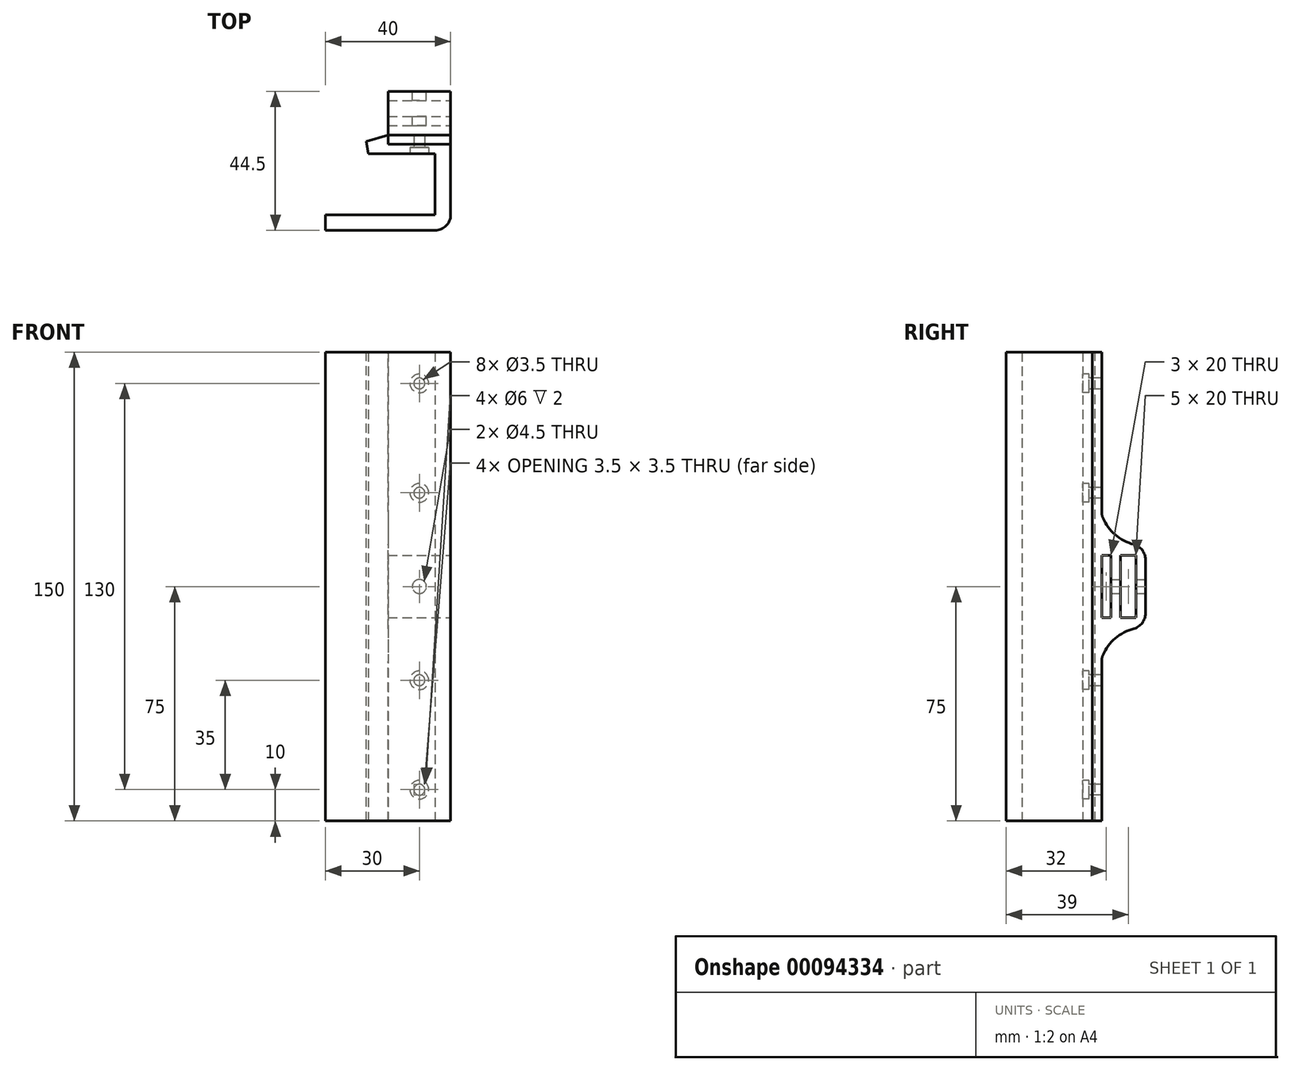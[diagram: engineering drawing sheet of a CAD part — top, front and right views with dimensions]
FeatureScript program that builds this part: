
annotation { "Feature Type Name" : "Feature", "Feature Type Description" : "" }
export const myFeature = defineFeature(function(context is Context, id is Id, definition is map)
    precondition{}
    {
        {
            var Q0;
            Q0=qCreatedBy(makeId("Top.planeOp"),FACE);
            var sketch = newSketch(context, id + "F0", { "sketchPlane" : qUnion([Q0])});
            skLineSegment(sketch, "E0", {"start": v(40, 0) * mm, "end": v(40, 27.5) * mm});
            skLineSegment(sketch, "E1", {"start": v(35, 24.5) * mm, "end": v(35, 5) * mm});
            skLineSegment(sketch, "E2", {"start": v(0, 0) * mm, "end": v(40, 0) * mm});
            skLineSegment(sketch, "E3", {"start": v(35, 5) * mm, "end": v(0, 5) * mm});
            skLineSegment(sketch, "E4", {"start": v(0, 5) * mm, "end": v(0, 0) * mm});
            skLineSegment(sketch, "E5", {"start": v(35, 24.5) * mm, "end": v(20, 24.5) * mm});
            skLineSegment(sketch, "E6", {"start": v(20, 24.5) * mm, "end": v(20, 27.5) * mm, "construction": true});
            skLineSegment(sketch, "E7", {"start": v(20, 27.5) * mm, "end": v(40, 27.5) * mm});
            skLineSegment(sketch, "E8", {"start": v(20, 24.5) * mm, "end": v(0, 24.5) * mm});
            skLineSegment(sketch, "E9", {"start": v(20, 27.5) * mm, "end": v(20, 30.5) * mm});
            skLineSegment(sketch, "E10", {"start": v(20, 30.5) * mm, "end": v(0, 24.5) * mm});
            skSolve(sketch);
        }
        {
            var Q0;
            Q0 = qSketchRegion(id + "F0", true);
            extrude(context, id + "F1", {"entities" : qUnion([Q0]), "depth" : 150 * mm});
        }
        {
            var Q0;
            Q0=makeQuery(id+"F1.opExtrude","SWEPT_FACE",FACE,{"disambiguationData":[OSD([sQuery(id+"F0.wireOp",EDGE,"E0")])]});
            var sketch = newSketch(context, id + "F2", { "sketchPlane" : qUnion([Q0])});
            skLineSegment(sketch, "E11", {"start": v(27.5, 150) * mm, "end": v(30.5, 150) * mm});
            skLineSegment(sketch, "E12", {"start": v(27.5, 0) * mm, "end": v(30.5, 0) * mm});
            skLineSegment(sketch, "E13", {"start": v(30.5, 0) * mm, "end": v(30.5, 62) * mm});
            skLineSegment(sketch, "E14", {"start": v(30.5, 62) * mm, "end": v(44.5, 62) * mm});
            skLineSegment(sketch, "E15", {"start": v(44.5, 62) * mm, "end": v(44.5, 88) * mm});
            skLineSegment(sketch, "E16", {"start": v(44.5, 88) * mm, "end": v(30.5, 88) * mm});
            skLineSegment(sketch, "E17", {"start": v(30.5, 88) * mm, "end": v(30.5, 150) * mm});
            skLineSegment(sketch, "E18.bottom", {"start": v(41.5, 85) * mm, "end": v(36.5, 85) * mm});
            skLineSegment(sketch, "E18.top", {"start": v(41.5, 65) * mm, "end": v(36.5, 65) * mm});
            skLineSegment(sketch, "E18.left", {"start": v(41.5, 85) * mm, "end": v(41.5, 65) * mm});
            skLineSegment(sketch, "E18.right", {"start": v(36.5, 85) * mm, "end": v(36.5, 65) * mm});
            skLineSegment(sketch, "E19.bottom", {"start": v(33.5, 85) * mm, "end": v(30.5, 85) * mm});
            skLineSegment(sketch, "E19.top", {"start": v(33.5, 65) * mm, "end": v(30.5, 65) * mm});
            skLineSegment(sketch, "E19.left", {"start": v(33.5, 85) * mm, "end": v(33.5, 65) * mm});
            skLineSegment(sketch, "E19.right", {"start": v(30.5, 85) * mm, "end": v(30.5, 65) * mm});
            skLineSegment(sketch, "E20", {"start": v(44.5, 75) * mm, "end": v(27.5, 75) * mm, "construction": true});
            skPoint(sketch, "E21", {"position": v(33.5, 75) * mm});
            skPoint(sketch, "E22", {"position": v(41.5, 75) * mm});
            skArc(sketch, "E23", {"start": v(30.5, 98) * mm, "mid": v(35.9, 90.76) * mm, "end": v(44.5, 88) * mm});
            skArc(sketch, "E24", {"start": v(44.5, 62) * mm, "mid": v(35.9, 59.24) * mm, "end": v(30.5, 52) * mm});
            skSolve(sketch);
        }
        {
            var Q0;
            Q0=makeQuery(id+"F2.imprint","IMPRINT",FACE,{"disambiguationData":[TD([[makeQuery(id+"F2.imprint","IMPRINT",EDGE,{"derivedFrom":sQuery(id+"F2.wireOp",EDGE,"E11")}),-1.0]])]});
            var Q1;
            {var subQ0=sQuery(id+"F2.wireOp",EDGE,"E16");Q1=makeQuery(id+"F2.imprint","IMPRINT",FACE,{"disambiguationData":[TD([[makeQuery(id+"F2.imprint","IMPRINT",EDGE,{"derivedFrom":subQ0}),-1.0]])]});}
            var Q2;
            {var subQ0=sQuery(id+"F2.wireOp",EDGE,"E14");Q2=makeQuery(id+"F2.imprint","IMPRINT",FACE,{"disambiguationData":[TD([[makeQuery(id+"F2.imprint","IMPRINT",EDGE,{"derivedFrom":subQ0}),-1.0]])]});}
            extrude(context, id + "F3", {"entities" : qUnion([Q0, Q1, Q2]), "oppositeDirection" : true, "depth" : 20 * mm});
        }
        {
            var Q0;
            Q0=makeQuery(id+"F1.opExtrude","SWEPT_FACE",FACE,{"disambiguationData":[OSD([sQuery(id+"F0.wireOp",EDGE,"E5"),sQuery(id+"F0.wireOp",EDGE,"E8")])]});
            var sketch = newSketch(context, id + "F4", { "sketchPlane" : qUnion([Q0])});
            skCircle(sketch, "E25", {"center": v(30, 140) * mm, "radius": 1.75 * mm});
            skCircle(sketch, "E26", {"center": v(30, 105) * mm, "radius": 1.75 * mm});
            skCircle(sketch, "E27", {"center": v(30, 45) * mm, "radius": 1.75 * mm});
            skCircle(sketch, "E28", {"center": v(30, 10) * mm, "radius": 1.75 * mm});
            skLineSegment(sketch, "E29", {"start": v(30, 140) * mm, "end": v(30, 2.8) * mm, "construction": true});
            skCircle(sketch, "E30", {"center": v(30, 140) * mm, "radius": 3 * mm});
            skCircle(sketch, "E31", {"center": v(30, 105) * mm, "radius": 3 * mm});
            skCircle(sketch, "E32", {"center": v(30, 45) * mm, "radius": 3 * mm});
            skCircle(sketch, "E33", {"center": v(30, 10) * mm, "radius": 3 * mm});
            skSolve(sketch);
        }
        {
            var Q0;
            Q0=makeQuery(id+"F4.imprint","IMPRINT",FACE,{"disambiguationData":[TD([[makeQuery(id+"F4.imprint","IMPRINT",EDGE,{"derivedFrom":sQuery(id+"F4.wireOp",EDGE,"E25")}),1.0]])]});
            var Q1;
            Q1=makeQuery(id+"F4.imprint","IMPRINT",FACE,{"disambiguationData":[TD([[makeQuery(id+"F4.imprint","IMPRINT",EDGE,{"derivedFrom":sQuery(id+"F4.wireOp",EDGE,"E26")}),1.0]])]});
            var Q2;
            Q2=makeQuery(id+"F4.imprint","IMPRINT",FACE,{"disambiguationData":[TD([[makeQuery(id+"F4.imprint","IMPRINT",EDGE,{"derivedFrom":sQuery(id+"F4.wireOp",EDGE,"E27")}),1.0]])]});
            var Q3;
            Q3=makeQuery(id+"F4.imprint","IMPRINT",FACE,{"disambiguationData":[TD([[makeQuery(id+"F4.imprint","IMPRINT",EDGE,{"derivedFrom":sQuery(id+"F4.wireOp",EDGE,"E28")}),1.0]])]});
            var Q4;
            Q4=makeQuery(id+"F3.opExtrude","SWEPT_FACE",FACE,{"disambiguationData":[OSD([sQuery(id+"F2.wireOp",EDGE,"E17")])]});
            extrude(context, id + "F5", {"entities" : qUnion([Q0, Q1, Q2, Q3]), "operationType" : NewBodyOperationType.REMOVE, "endBound" : BoundingType.UP_TO_SURFACE, "oppositeDirection" : true, "endBoundEntityFace" : qUnion([Q4]), "depth" : 25 * mm});
        }
        {
            var Q0;
            Q0=makeQuery(id+"F3.opExtrude","SWEPT_FACE",FACE,{"disambiguationData":[OSD([sQuery(id+"F2.wireOp",EDGE,"E15")])]});
            var sketch = newSketch(context, id + "F6", { "sketchPlane" : qUnion([Q0])});
            skCircle(sketch, "E34", {"center": v(-30, 75) * mm, "radius": 2.25 * mm});
            skLineSegment(sketch, "E35", {"start": v(-20, 88) * mm, "end": v(-40, 62) * mm, "construction": true});
            skSolve(sketch);
        }
        {
            var Q0;
            Q0 = qSketchRegion(id + "F6", true);
            var Q1;
            Q1=makeQuery(id+"F3.opExtrude","SWEPT_FACE",FACE,{"disambiguationData":[OSD([sQuery(id+"F2.wireOp",EDGE,"E19.right")])]});
            extrude(context, id + "F7", {"entities" : qUnion([Q0]), "operationType" : NewBodyOperationType.REMOVE, "endBound" : BoundingType.UP_TO_SURFACE, "oppositeDirection" : true, "endBoundEntityFace" : qUnion([Q1]), "depth" : 25 * mm});
        }
        {
            var Q0;
            Q0=makeQuery(id+"F3.opExtrude","SWEPT_EDGE",EDGE,{"disambiguationData":[OSD([sQuery(id+"F2.wireOp",EDGE,"E17"),sQuery(id+"F2.wireOp",EDGE,"E23")])]});
            var Q1;
            Q1=makeQuery(id+"F3.opExtrude","SWEPT_EDGE",EDGE,{"disambiguationData":[OSD([sQuery(id+"F2.wireOp",EDGE,"E13"),sQuery(id+"F2.wireOp",EDGE,"E24")])]});
            var Q2;
            Q2=makeQuery(id+"F3.opExtrude","SWEPT_EDGE",EDGE,{"disambiguationData":[OSD([sQuery(id+"F2.wireOp",EDGE,"E15"),sQuery(id+"F2.wireOp",EDGE,"E16"),sQuery(id+"F2.wireOp",EDGE,"E23")])]});
            var Q3;
            Q3=makeQuery(id+"F3.opExtrude","SWEPT_EDGE",EDGE,{"disambiguationData":[OSD([sQuery(id+"F2.wireOp",EDGE,"E14"),sQuery(id+"F2.wireOp",EDGE,"E15"),sQuery(id+"F2.wireOp",EDGE,"E24")])]});
            fillet(context, id + "F8", {"entities" : qUnion([Q0, Q1, Q2, Q3]), "radius" : 5 * mm, "tangentPropagation" : true, "allowEdgeOverflow" : false});
        }
        {
            var Q0;
            Q0=makeQuery(id+"F4.imprint","IMPRINT",FACE,{"disambiguationData":[TD([[makeQuery(id+"F4.imprint","IMPRINT",EDGE,{"derivedFrom":sQuery(id+"F4.wireOp",EDGE,"E25")}),-1.0]])]});
            var Q1;
            Q1=makeQuery(id+"F4.imprint","IMPRINT",FACE,{"disambiguationData":[TD([[makeQuery(id+"F4.imprint","IMPRINT",EDGE,{"derivedFrom":sQuery(id+"F4.wireOp",EDGE,"E26")}),-1.0]])]});
            var Q2;
            Q2=makeQuery(id+"F4.imprint","IMPRINT",FACE,{"disambiguationData":[TD([[makeQuery(id+"F4.imprint","IMPRINT",EDGE,{"derivedFrom":sQuery(id+"F4.wireOp",EDGE,"E27")}),-1.0]])]});
            var Q3;
            Q3=makeQuery(id+"F4.imprint","IMPRINT",FACE,{"disambiguationData":[TD([[makeQuery(id+"F4.imprint","IMPRINT",EDGE,{"derivedFrom":sQuery(id+"F4.wireOp",EDGE,"E28")}),-1.0]])]});
            extrude(context, id + "F9", {"entities" : qUnion([Q0, Q1, Q2, Q3]), "operationType" : NewBodyOperationType.REMOVE, "oppositeDirection" : true, "depth" : 2 * mm});
        }
        {
            var Q0;
            Q0=makeQuery(id+"F1.opExtrude","SWEPT_EDGE",EDGE,{"disambiguationData":[OSD([sQuery(id+"F0.wireOp",EDGE,"E0"),sQuery(id+"F0.wireOp",EDGE,"E2")])]});
            fillet(context, id + "F10", {"entities" : qUnion([Q0]), "radius" : 5 * mm, "tangentPropagation" : true, "allowEdgeOverflow" : false});
        }
        {
            var Q0;
            Q0=makeQuery(id+"F1.opExtrude","SWEPT_EDGE",EDGE,{"disambiguationData":[OSD([sQuery(id+"F0.wireOp",EDGE,"E8"),sQuery(id+"F0.wireOp",EDGE,"E10")])]});
            chamfer(context, id + "F11", {"entities" : qUnion([Q0]), "width" : 2 * mm, "tangentPropagation" : true});
        }
    });
